# Revit family: Haworth_Belong_Tool_TrayShelf
name_source: partatom
category: Furniture Systems
revit_build: Autodesk Revit 2018 (Build: 20170223_1515(x64)
units: mm (PartAtom-declared; Revit-internal decimal feet)

## family parameters
Always vertical = Yes
Cut with Voids When Loaded = No
OmniClass Number = 23.40.70.14.64.21
OmniClass Title = Systems Furniture
Part Type = Normal
Room Calculation Point = No
Round Connector Dimension = Use Diameter
Shared = No
Work Plane-Based = No

## types (3) — shared parameters
Assembly Code = E2020200
Description = Haworth - Belong Tools - Tray Shelf
Manufacturer = Haworth
Model = Haworth - Belong Tools - Tray Shelf
Revision Number = 2
Shelf Finish = Haworth _ Paint _ Graphite
Size = Verify Final Dim. w/ Haworth
Sustainability Info = https://www.haworth.com
URL = www.haworth.com
URL - Product = http://www.haworth.com
Warranty = http://www.haworth.com

## per-type parameters (varying)
| type | Actual Depth | Actual Height | Actual Width | Back Offset | Hanging Support |
| Hanging Document Tray | 8 7/8" | 1 1/2" | 12 3/4" | 0" | Yes |
| Hanging Mini Shelf | 4" | 1" | 8" | 0" | Yes |
| Freestanding Document Tray | 8 7/8" | 2 1/2" | 12 3/4" | 1/4" | No |

type visibility flags: 3 boolean params named "<type name>" — each type sets only its own to Yes (folded from table)

## geometry (parser evidence)
native form markers: Sweep x3
no freeform markers — native parametric forms only
